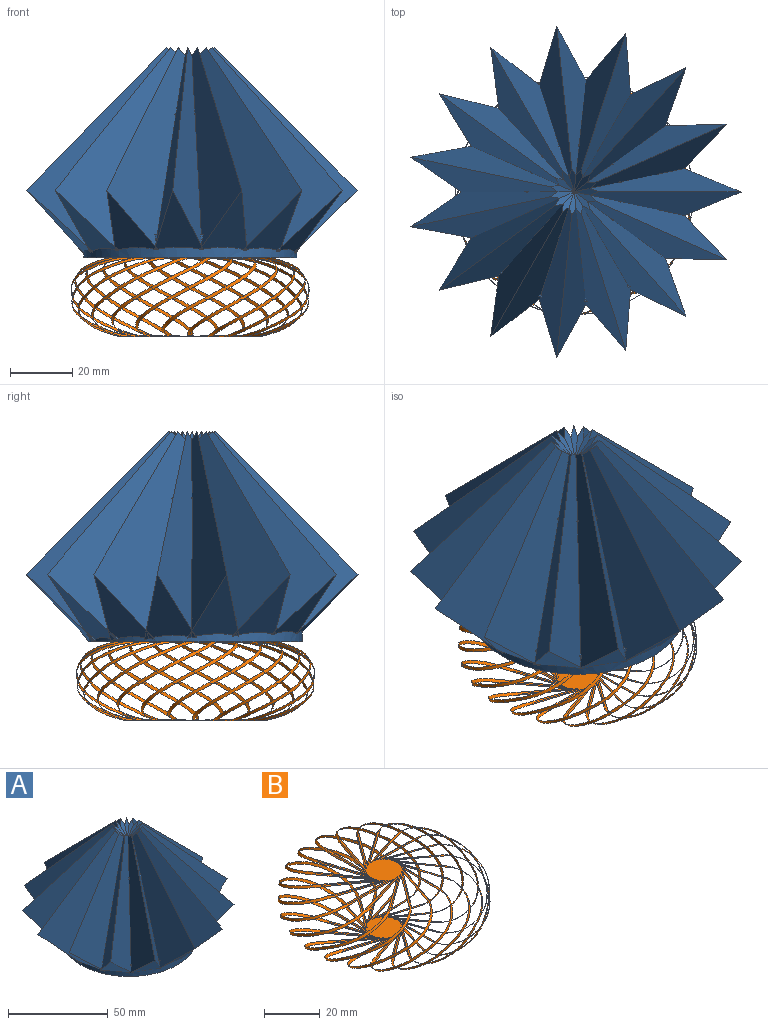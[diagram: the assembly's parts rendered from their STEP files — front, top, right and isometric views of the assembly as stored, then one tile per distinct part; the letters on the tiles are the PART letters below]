
ASSEMBLY  parts=2 mates=1
PART A: 221 faces, bbox 105.8x106.4x67.4 mm
  f0: plane 0.49x0.29mm, normal (-0.47,0.53,-0.71), area 0.1mm2, adj f11,f160,f202
  f1: plane 0.49x0.29mm, normal (-0.47,-0.53,-0.71), area 0.1mm2, adj f12,f46,f200
  f2: plane 0.47x0.29mm, normal (0.57,0.42,-0.71), area 0.1mm2, adj f3,f27,f198
  f3: plane 0.99x0.77mm, normal (0.57,0.42,0.71), area 0.1mm2, adj f2,f26,f198
  f4: plane 0.99x0.77mm, normal (0.57,-0.42,0.71), area 0.1mm2, adj f5,f157,f197
  f5: plane 0.47x0.29mm, normal (0.57,-0.42,-0.71), area 0.1mm2, adj f4,f161,f197
  f6: plane 0.26x0.22mm, normal (0,0,1), area 0mm2, adj f15,f16,f197
  f7: plane 7.69x7.02mm, normal (-0.65,-0.29,0.71), area 11.7mm2, adj f13,f20,f28,f195
  f8: plane 7.69x7.02mm, normal (-0.65,0.29,0.71), area 11.7mm2, adj f15,f91,f117,f195
  f9: plane 63.99x38.53mm, normal (-0.72,0.66,0.2), area 991.9mm2, adj f46,f60,f96,f97,f105,f127,f199,f200
  f10: plane 63.99x38.53mm, normal (-0.72,-0.66,0.2), area 992.1mm2, adj f88,f92,f93,f160,f201,f202
  f11: plane 0.98x0.77mm, normal (-0.47,0.53,0.71), area 0.1mm2, adj f0,f160,f201
  f12: plane 0.98x0.77mm, normal (-0.47,-0.53,0.71), area 0.1mm2, adj f1,f46,f199
  f13: plane 63.99x43.79mm, normal (0.57,-0.8,0.2), area 992.1mm2, adj f7,f14,f20,f26,f27,f198
  f14: plane 20.83x20.43mm, normal (0.65,0.29,-0.71), area 226.8mm2, adj f13,f17,f20,f36,f194
  f15: plane 63.99x43.79mm, normal (0.57,0.8,0.2), area 992mm2, adj f6,f8,f16,f18,f91,f157,f161,f197
  f16: cylinder r=34.13mm len=0.5mm, axis (0,0,-1), area 0.1mm2, adj f6,f15,f197
  f17: cylinder r=34.13mm len=68.25mm, axis (0,0,-1), area 418mm2, adj f14,f18,f19,f21,f29,f35,f36,f38
  f18: plane 20.26x19.65mm, normal (0.65,-0.29,-0.71), area 211.4mm2, adj f15,f17,f91,f152,f192
  f19: plane 2.46x1.93mm, normal (0.57,-0.8,0.2), area 0.7mm2, adj f17,f21,f196
  f20: plane 63.99x44.67mm, normal (-0.21,0.96,0.2), area 992.1mm2, adj f7,f13,f14,f24,f25,f34
  f21: plane 2.48x2.18mm, normal (0.65,0.29,-0.71), area 2.3mm2, adj f17,f19,f193
  f22: plane 0.42x0.29mm, normal (-0.65,0.29,-0.71), area 0.1mm2, adj f31,f111,f188
  f23: plane 0.47x0.29mm, normal (-0.22,-0.67,-0.71), area 0.1mm2, adj f33,f60,f186
  f24: plane 0.49x0.29mm, normal (0.35,0.61,-0.71), area 0.1mm2, adj f20,f25,f43
  f25: plane 0.92x0.77mm, normal (0.35,0.61,0.71), area 0.1mm2, adj f20,f24,f42
  f26: plane 0.89x0.77mm, normal (0.69,-0.15,0.71), area 0.1mm2, adj f3,f13,f27
  f27: plane 0.36x0.33mm, normal (0.69,-0.15,-0.71), area 0.1mm2, adj f2,f13,f26
  f28: plane 7.69x5.71mm, normal (-0.47,-0.53,0.71), area 11.7mm2, adj f7,f34,f37,f44
  f29: plane 2.02x1.58mm, normal (0.57,0.8,0.2), area 0.5mm2, adj f17,f153,f196
  f30: plane 63.99x42.47mm, normal (-0.93,0.31,0.2), area 991.3mm2, adj f60,f74,f98,f99,f100,f132,f185,f186
  f31: plane 0.96x0.77mm, normal (-0.65,0.29,0.71), area 0.1mm2, adj f22,f111,f187
  f32: plane 63.99x47.13mm, normal (-0.39,-0.9,0.2), area 992.1mm2, adj f103,f104,f111,f158,f159,f160,f187,f188
  f33: plane 0.83x0.77mm, normal (-0.22,-0.67,0.71), area 0.1mm2, adj f23,f60,f185
  f34: plane 63.99x36.7mm, normal (0.85,-0.5,0.2), area 992.1mm2, adj f20,f28,f35,f37,f42,f43
  f35: plane 20.71x18.76mm, normal (0.47,0.53,-0.71), area 232.5mm2, adj f17,f34,f37,f50,f190
  f36: plane 3.02x2.96mm, normal (0.85,-0.5,0.2), area 1.1mm2, adj f14,f17,f38
  f37: plane 63.99x35.26mm, normal (-0.58,0.79,0.2), area 992.1mm2, adj f28,f34,f35,f40,f41,f48
  f38: plane 3.02x2.96mm, normal (0.47,0.53,-0.71), area 3.4mm2, adj f17,f36,f189
  f39: plane 0.37x0.33mm, normal (0.07,-0.7,-0.71), area 0.1mm2, adj f47,f74,f181
  f40: plane 0.43x0.29mm, normal (0.07,0.7,-0.71), area 0.1mm2, adj f37,f41,f57
  f41: plane 0.77x0.73mm, normal (0.07,0.7,0.71), area 0.1mm2, adj f37,f40,f56
  f42: plane 0.77x0.77mm, normal (0.69,0.15,0.71), area 0.1mm2, adj f25,f34,f43
  f43: plane 0.45x0.29mm, normal (0.69,0.15,-0.71), area 0.1mm2, adj f24,f34,f42
  f44: plane 7.69x7.31mm, normal (-0.22,-0.67,0.71), area 11.7mm2, adj f28,f48,f51,f58
  f45: plane 63.99x48.26mm, normal (-0.98,-0.1,0.2), area 990.7mm2, adj f74,f90,f101,f102,f108,f137,f180,f181
  f46: plane 63.99x47.58mm, normal (0.01,-0.98,0.2), area 991.9mm2, adj f1,f9,f12,f96,f97,f111,f112,f122
  f47: plane 0.83x0.77mm, normal (0.07,-0.7,0.71), area 0.1mm2, adj f39,f74,f180
  f48: plane 63.99x46.38mm, normal (0.97,-0.11,0.2), area 992.1mm2, adj f37,f44,f49,f51,f56,f57
  f49: plane 21.3x20.86mm, normal (0.22,0.67,-0.71), area 235.8mm2, adj f17,f48,f51,f64,f184
  f50: plane 3.6x3.34mm, normal (0.97,-0.11,0.2), area 1.3mm2, adj f17,f35,f52
  f51: plane 63.99x45.71mm, normal (-0.85,0.48,0.2), area 992.1mm2, adj f44,f48,f49,f54,f55,f62
  f52: plane 3.6x3.34mm, normal (0.22,0.67,-0.71), area 4.2mm2, adj f17,f50,f182
  f53: plane 0.45x0.29mm, normal (0.35,-0.61,-0.71), area 0.1mm2, adj f61,f90,f176
  f54: plane 0.4x0.29mm, normal (-0.22,0.67,-0.71), area 0.1mm2, adj f51,f55,f72
  f55: plane 0.93x0.77mm, normal (-0.22,0.67,0.71), area 0.1mm2, adj f51,f54,f71
  f56: plane 0.95x0.77mm, normal (0.57,0.42,0.71), area 0.1mm2, adj f41,f48,f57
  f57: plane 0.49x0.29mm, normal (0.57,0.42,-0.71), area 0.1mm2, adj f40,f48,f56
  f58: plane 7.69x7.64mm, normal (0.07,-0.7,0.71), area 11.7mm2, adj f44,f62,f66,f73
  f59: plane 63.99x45.71mm, normal (-0.85,-0.48,0.2), area 990.6mm2, adj f90,f106,f107,f113,f142,f147,f175,f176
  f60: plane 63.99x39.8mm, normal (0.4,-0.89,0.2), area 991.3mm2, adj f9,f23,f30,f33,f98,f99,f105,f127
  f61: plane 0.98x0.77mm, normal (0.35,-0.61,0.71), area 0.1mm2, adj f53,f90,f175
  f62: plane 63.99x48.04mm, normal (0.93,0.3,0.2), area 992.1mm2, adj f51,f58,f63,f66,f71,f72
  f63: plane 21.24x20.87mm, normal (-0.07,0.7,-0.71), area 236.5mm2, adj f17,f62,f66,f80,f179
  f64: plane 3.36x3.35mm, normal (0.93,0.3,0.2), area 1.5mm2, adj f17,f49,f65,f67
  f65: plane 0.6x0.16mm, normal (0.07,-0.7,-0.71), area 0.1mm2, adj f17,f64,f67
  f66: plane 63.99x48.26mm, normal (-0.98,0.1,0.2), area 992.1mm2, adj f58,f62,f63,f69,f70,f77
  f67: plane 3.38x3.28mm, normal (-0.07,0.7,-0.71), area 4.6mm2, adj f17,f64,f65,f177
  f68: plane 0.49x0.29mm, normal (0.57,-0.42,-0.71), area 0.1mm2, adj f76,f147,f171
  f69: plane 0.48x0.29mm, normal (-0.47,0.53,-0.71), area 0.1mm2, adj f66,f70,f87
  f70: plane 0.99x0.77mm, normal (-0.47,0.53,0.71), area 0.1mm2, adj f66,f69,f86
  f71: plane 0.98x0.77mm, normal (0.35,0.61,0.71), area 0.1mm2, adj f55,f62,f72
  f72: plane 0.45x0.29mm, normal (0.35,0.61,-0.71), area 0.1mm2, adj f54,f62,f71
  f73: plane 7.69x6.66mm, normal (0.35,-0.61,0.71), area 11.7mm2, adj f58,f77,f79,f88
  f74: plane 63.99x41.39mm, normal (0.73,-0.65,0.2), area 990.7mm2, adj f30,f39,f45,f47,f100,f101,f102,f132
  f75: plane 63.99x35.26mm, normal (-0.58,-0.79,0.2), area 991mm2, adj f114,f115,f116,f117,f147,f148,f170,f171
  f76: plane 0.95x0.77mm, normal (0.57,-0.42,0.71), area 0.1mm2, adj f68,f147,f170
  f77: plane 63.99x41.39mm, normal (0.73,0.65,0.2), area 992.1mm2, adj f66,f73,f78,f79,f86,f87
  f78: plane 20.8x20.45mm, normal (-0.35,0.61,-0.71), area 234.5mm2, adj f17,f77,f79,f94,f174
  f79: plane 63.99x42.47mm, normal (-0.93,-0.31,0.2), area 992.1mm2, adj f73,f77,f78,f84,f85,f92
  f80: plane 3.36x2.95mm, normal (0.73,0.65,0.2), area 1.5mm2, adj f17,f63,f81,f82
  f81: plane 0.48x0.24mm, normal (0.35,-0.61,-0.71), area 0mm2, adj f17,f80,f82
  f82: plane 3.38x2.92mm, normal (-0.35,0.61,-0.71), area 4.5mm2, adj f17,f80,f81,f172
  f83: plane 0.45x0.29mm, normal (0.69,-0.15,-0.71), area 0.1mm2, adj f89,f114,f167
  f84: plane 0.48x0.29mm, normal (-0.65,0.29,-0.71), area 0.1mm2, adj f79,f85,f162
  f85: plane 0.88x0.77mm, normal (-0.65,0.29,0.71), area 0.1mm2, adj f79,f84,f163
  f86: plane 0.83x0.77mm, normal (0.07,0.7,0.71), area 0.1mm2, adj f70,f77,f87
  f87: plane 0.37x0.33mm, normal (0.07,0.7,-0.71), area 0.1mm2, adj f69,f77,f86
  f88: plane 7.69x6.22mm, normal (0.57,-0.42,0.71), area 11.7mm2, adj f10,f73,f92,f159
  f89: plane 0.77x0.77mm, normal (0.69,-0.15,0.71), area 0.1mm2, adj f83,f114,f166
  f90: plane 63.99x48.04mm, normal (0.93,-0.3,0.2), area 990.6mm2, adj f45,f53,f59,f61,f106,f107,f108,f137
  f91: plane 63.99x44.67mm, normal (-0.21,-0.96,0.2), area 991.6mm2, adj f8,f15,f18,f109,f110,f114,f166,f167
  f92: plane 63.99x39.8mm, normal (0.4,0.89,0.2), area 992.1mm2, adj f10,f79,f88,f93,f162,f163
  f93: plane 20.58x19.7mm, normal (-0.57,0.42,-0.71), area 229.9mm2, adj f10,f17,f92,f156,f169
  f94: plane 3.44x3.27mm, normal (0.4,0.89,0.2), area 1.3mm2, adj f17,f78,f95
  f95: plane 3.44x3.27mm, normal (-0.57,0.42,-0.71), area 4mm2, adj f17,f94,f168
  f96: cylinder r=34.13mm len=0.95mm, axis (0,0,-1), area 0.2mm2, adj f9,f46,f97
  f97: plane 0.52x0.39mm, normal (0,0,1), area 0.1mm2, adj f9,f46,f96
  f98: cylinder r=34.13mm len=1.73mm, axis (0,0,-1), area 0.7mm2, adj f30,f60,f99
  f99: plane 0.91x0.86mm, normal (0,0,1), area 0.3mm2, adj f30,f60,f98
  f100: plane 7.69x6.66mm, normal (0.35,0.61,0.71), area 11.7mm2, adj f30,f74,f105,f108
  f101: cylinder r=34.13mm len=2.22mm, axis (0,0,-1), area 1.1mm2, adj f45,f74,f102
  f102: plane 1.22x0.93mm, normal (0,0,1), area 0.5mm2, adj f45,f74,f101
  f103: plane 0.01x0.01mm, normal (0,0,1), area 0mm2, adj f32,f104,f111
  f104: cylinder r=34.13mm len=0.02mm, axis (0,0,-1), area 0mm2, adj f32,f103,f111
  f105: plane 7.69x6.22mm, normal (0.57,0.42,0.71), area 11.7mm2, adj f9,f60,f100,f112
  f106: cylinder r=34.13mm len=2.32mm, axis (0,0,-1), area 1.2mm2, adj f59,f90,f107
  f107: plane 1.21x1.01mm, normal (0,0,1), area 0.6mm2, adj f59,f90,f106
  f108: plane 7.69x7.64mm, normal (0.07,0.7,0.71), area 11.7mm2, adj f45,f90,f100,f113
  f109: cylinder r=34.13mm len=1.37mm, axis (0,0,-1), area 0.4mm2, adj f91,f110,f114
  f110: plane 0.73x0.66mm, normal (0,0,1), area 0.2mm2, adj f91,f109,f114
  f111: plane 63.99x47.13mm, normal (-0.39,0.9,0.2), area 992.1mm2, adj f22,f31,f32,f46,f103,f104,f112,f122
  f112: plane 7.69x7.52mm, normal (0.69,0.15,0.71), area 11.7mm2, adj f46,f105,f111,f159
  f113: plane 7.69x7.31mm, normal (-0.22,0.67,0.71), area 11.7mm2, adj f59,f108,f117,f147
  f114: plane 63.99x36.7mm, normal (0.85,0.5,0.2), area 991.6mm2, adj f75,f83,f89,f91,f109,f110,f117,f148
  f115: cylinder r=34.13mm len=2.02mm, axis (0,0,-1), area 0.9mm2, adj f75,f116,f147
  f116: plane 1.11x0.89mm, normal (0,0,1), area 0.5mm2, adj f75,f115,f147
  f117: plane 7.69x5.71mm, normal (-0.47,0.53,0.71), area 11.7mm2, adj f8,f75,f113,f114
  f118: plane 2.3x2.05mm, normal (-0.39,0.9,0.2), area 0.6mm2, adj f17,f119,f158
  f119: plane 2.32x2.07mm, normal (-0.69,-0.15,-0.71), area 2mm2, adj f17,f118,f120
  f120: plane 2.21x1.99mm, normal (-0.69,0.15,-0.71), area 1.9mm2, adj f17,f119,f121
  f121: plane 2.19x1.96mm, normal (-0.39,-0.9,0.2), area 0.6mm2, adj f17,f120,f122
  f122: plane 20.37x19.85mm, normal (-0.69,-0.15,-0.71), area 215.4mm2, adj f17,f46,f111,f121,f123
  f123: plane 1.75x1.61mm, normal (-0.72,0.66,0.2), area 0.4mm2, adj f17,f122,f124
  f124: plane 1.75x1.62mm, normal (-0.57,-0.42,-0.71), area 1.1mm2, adj f17,f123,f125
  f125: plane 1.79x1.68mm, normal (-0.69,-0.15,-0.71), area 1.1mm2, adj f17,f124,f126
  f126: plane 1.78x1.67mm, normal (0.01,-0.98,0.2), area 0.3mm2, adj f17,f125,f127
  f127: plane 19.46x19.36mm, normal (-0.57,-0.42,-0.71), area 207.6mm2, adj f9,f17,f60,f126,f128
  f128: plane 1.37x1.28mm, normal (-0.93,0.31,0.2), area 0.2mm2, adj f17,f127,f129
  f129: plane 1.38x1.28mm, normal (-0.35,-0.61,-0.71), area 0.6mm2, adj f17,f128,f130
  f130: plane 1.31x1.25mm, normal (-0.57,-0.42,-0.71), area 0.6mm2, adj f17,f129,f131
  f131: plane 1.31x1.24mm, normal (0.4,-0.89,0.2), area 0.2mm2, adj f17,f130,f132
  f132: plane 19.86x19.13mm, normal (-0.35,-0.61,-0.71), area 201.6mm2, adj f17,f30,f74,f131,f133
  f133: plane 1.03x0.99mm, normal (-0.98,-0.1,0.2), area 0.1mm2, adj f17,f132,f134
  f134: plane 1.03x0.99mm, normal (-0.07,-0.7,-0.71), area 0.4mm2, adj f17,f133,f135
  f135: plane 0.98x0.84mm, normal (-0.35,-0.61,-0.71), area 0.4mm2, adj f17,f134,f136
  f136: plane 0.98x0.84mm, normal (0.73,-0.65,0.2), area 0.1mm2, adj f17,f135,f137
  f137: plane 19.53x18.93mm, normal (-0.07,-0.7,-0.71), area 198.7mm2, adj f17,f45,f90,f136,f138
  f138: plane 0.92x0.76mm, normal (-0.85,-0.48,0.2), area 0.1mm2, adj f17,f137,f139
  f139: plane 0.92x0.82mm, normal (0.22,-0.67,-0.71), area 0.3mm2, adj f17,f138,f140
  f140: plane 0.93x0.88mm, normal (-0.07,-0.7,-0.71), area 0.3mm2, adj f17,f139,f141
  f141: plane 0.93x0.88mm, normal (0.93,-0.3,0.2), area 0.1mm2, adj f17,f140,f142
  f142: plane 20.15x19.01mm, normal (0.22,-0.67,-0.71), area 199.7mm2, adj f17,f59,f141,f143,f147
  f143: plane 1.08x1.06mm, normal (-0.58,-0.79,0.2), area 0.1mm2, adj f17,f142,f144
  f144: plane 1.09x1.06mm, normal (0.47,-0.53,-0.71), area 0.5mm2, adj f17,f143,f145
  f145: plane 1.2x1.11mm, normal (0.22,-0.67,-0.71), area 0.5mm2, adj f17,f144,f146
  f146: plane 1.2x1.11mm, normal (0.97,0.11,0.2), area 0.1mm2, adj f17,f145,f148
  f147: plane 63.99x46.38mm, normal (0.97,0.11,0.2), area 991mm2, adj f59,f68,f75,f76,f113,f115,f116,f142
  f148: plane 19.28x18.64mm, normal (0.47,-0.53,-0.71), area 204.3mm2, adj f17,f75,f114,f146,f149
  f149: plane 1.56x1.44mm, normal (-0.21,-0.96,0.2), area 0.3mm2, adj f17,f148,f150
  f150: plane 1.56x1.45mm, normal (0.65,-0.29,-0.71), area 0.8mm2, adj f17,f149,f151
  f151: plane 1.53x1.5mm, normal (0.47,-0.53,-0.71), area 0.8mm2, adj f17,f150,f152
  f152: plane 1.52x1.5mm, normal (0.85,0.5,0.2), area 0.3mm2, adj f17,f18,f151
  f153: plane 2.03x1.71mm, normal (0.65,-0.29,-0.71), area 1.5mm2, adj f17,f29,f191
  f154: plane 68.25x68.25mm, normal (0,0,-1), area 3658.9mm2, adj f17
  f155: plane 3.02x2.84mm, normal (-0.69,0.15,-0.71), area 3mm2, adj f17,f156,f164
  f156: plane 3.03x2.84mm, normal (0.01,0.98,0.2), area 1mm2, adj f17,f93,f155
  f157: plane 0.89x0.77mm, normal (0.69,0.15,0.71), area 0.1mm2, adj f4,f15,f161
  f158: plane 20.95x20.25mm, normal (-0.69,0.15,-0.71), area 223.3mm2, adj f17,f32,f118,f160,f165
  f159: plane 7.69x7.52mm, normal (0.69,-0.15,0.71), area 11.7mm2, adj f32,f88,f112,f160
  f160: plane 63.99x47.58mm, normal (0.01,0.98,0.2), area 992.1mm2, adj f0,f10,f11,f32,f158,f159
  f161: plane 0.36x0.33mm, normal (0.69,0.15,-0.71), area 0.1mm2, adj f5,f15,f157
  f162: plane 0.47x0.29mm, normal (-0.22,0.67,-0.71), area 0.1mm2, adj f84,f92,f163
  f163: plane 0.83x0.77mm, normal (-0.22,0.67,0.71), area 0.1mm2, adj f85,f92,f162
  f164: plane 2.74x2.53mm, normal (-0.57,0.42,-0.71), area 2.9mm2, adj f17,f155,f165
  f165: plane 2.72x2.51mm, normal (-0.72,-0.66,0.2), area 0.9mm2, adj f17,f158,f164
  f166: plane 0.92x0.77mm, normal (0.35,-0.61,0.71), area 0.1mm2, adj f89,f91,f167
  f167: plane 0.49x0.29mm, normal (0.35,-0.61,-0.71), area 0.1mm2, adj f83,f91,f166
  f168: plane 3.4x3.17mm, normal (-0.35,0.61,-0.71), area 3.8mm2, adj f17,f95,f169
  f169: plane 3.4x3.17mm, normal (-0.93,-0.31,0.2), area 1.2mm2, adj f17,f93,f168
  f170: plane 0.77x0.73mm, normal (0.07,-0.7,0.71), area 0.1mm2, adj f75,f76,f171
  f171: plane 0.43x0.29mm, normal (0.07,-0.7,-0.71), area 0.1mm2, adj f68,f75,f170
  f172: plane 3.49x3.36mm, normal (-0.07,0.7,-0.71), area 4.5mm2, adj f17,f82,f173,f174
  f173: plane 0.34x0.13mm, normal (0.07,-0.7,-0.71), area 0mm2, adj f17,f172,f174
  f174: plane 3.58x3.36mm, normal (-0.98,0.1,0.2), area 1.4mm2, adj f17,f78,f172,f173
  f175: plane 0.93x0.77mm, normal (-0.22,-0.67,0.71), area 0.1mm2, adj f59,f61,f176
  f176: plane 0.4x0.29mm, normal (-0.22,-0.67,-0.71), area 0.1mm2, adj f53,f59,f175
  f177: plane 3.38x3.09mm, normal (0.22,0.67,-0.71), area 4.6mm2, adj f17,f67,f178,f179
  f178: plane 0.65x0.2mm, normal (-0.22,-0.67,-0.71), area 0.1mm2, adj f17,f177,f179
  f179: plane 3.36x2.94mm, normal (-0.85,0.48,0.2), area 1.5mm2, adj f17,f63,f177,f178
  f180: plane 0.99x0.77mm, normal (-0.47,-0.53,0.71), area 0.1mm2, adj f45,f47,f181
  f181: plane 0.48x0.29mm, normal (-0.47,-0.53,-0.71), area 0.1mm2, adj f39,f45,f180
  f182: plane 3.36x3.28mm, normal (0.47,0.53,-0.71), area 4.3mm2, adj f17,f52,f183,f184
  f183: plane 0.16x0.12mm, normal (-0.47,-0.53,-0.71), area 0mm2, adj f17,f182,f184
  f184: plane 3.36x3.32mm, normal (-0.58,0.79,0.2), area 1.4mm2, adj f17,f49,f182,f183
  f185: plane 0.88x0.77mm, normal (-0.65,-0.29,0.71), area 0.1mm2, adj f30,f33,f186
  f186: plane 0.48x0.29mm, normal (-0.65,-0.29,-0.71), area 0.1mm2, adj f23,f30,f185
  f187: plane 0.96x0.77mm, normal (-0.65,-0.29,0.71), area 0.1mm2, adj f31,f32,f188
  f188: plane 0.42x0.29mm, normal (-0.65,-0.29,-0.71), area 0.1mm2, adj f22,f32,f187
  f189: plane 3.33x3.08mm, normal (0.65,0.29,-0.71), area 3.5mm2, adj f17,f38,f190
  f190: plane 3.33x3.08mm, normal (-0.21,0.96,0.2), area 1.1mm2, adj f17,f35,f189
  f191: plane 1.94x1.94mm, normal (0.71,0,-0.71), area 1.4mm2, adj f17,f153,f192
  f192: plane 1.93x1.93mm, normal (0.2,-0.96,0.2), area 0.4mm2, adj f17,f18,f191
  f193: plane 2.6x2.6mm, normal (0.71,0,-0.71), area 2.5mm2, adj f17,f21,f194
  f194: plane 2.58x2.58mm, normal (0.2,0.96,0.2), area 0.8mm2, adj f14,f17,f193
  f195: plane 7.69x7.69mm, normal (-0.71,0,0.71), area 11.7mm2, adj f7,f8,f197,f198
  f196: plane 20.05x20.05mm, normal (0.71,0,-0.71), area 219.4mm2, adj f17,f19,f29,f197,f198
  f197: plane 63.99x48.41mm, normal (0.2,-0.96,0.2), area 992.1mm2, adj f4,f5,f6,f15,f16,f195,f196,f198
  f198: plane 63.99x48.41mm, normal (0.2,0.96,0.2), area 992.1mm2, adj f2,f3,f13,f195,f196,f197
  f199: plane 0.77x0.77mm, normal (-0.71,0,0.71), area 0.1mm2, adj f9,f12,f200
  f200: plane 0.4x0.29mm, normal (-0.71,0,-0.71), area 0.1mm2, adj f1,f9,f199
  f201: plane 0.77x0.77mm, normal (-0.71,0,0.71), area 0.1mm2, adj f10,f11,f202
  f202: plane 0.4x0.29mm, normal (-0.71,0,-0.71), area 0.1mm2, adj f0,f10,f201
  f203: cylinder r=19.05mm len=38.1mm, axis (0,0,-1), area 531.2mm2, adj f204,f205,f206,f208,f209,f210,f211,f212
  f204: plane 10.47x5.99mm, normal (-0.71,0,-0.71), area 74.7mm2, adj f203,f206,f207,f208
  f205: plane 38.1x38.1mm, normal (0,0,-1), area 1140.1mm2, adj f203
  f206: plane 10.83x9.21mm, normal (-0.65,0.29,-0.71), area 74.7mm2, adj f203,f204,f207,f212
  f207: plane 50.06x49.79mm, normal (0,0,1), area 1932.4mm2, adj f204,f206,f208,f209,f210,f211,f212,f213
  f208: plane 10.83x9.21mm, normal (-0.65,-0.29,-0.71), area 74.7mm2, adj f203,f204,f207,f220
  f209: plane 10.24x7.77mm, normal (0.69,0.15,-0.71), area 74.7mm2, adj f203,f207,f214,f215
  f210: plane 10.95x9.78mm, normal (0.35,0.61,-0.71), area 74.7mm2, adj f203,f207,f211,f214
  f211: plane 10.41x6.91mm, normal (0.07,0.7,-0.71), area 74.7mm2, adj f203,f207,f210,f213
  f212: plane 10.84x10.6mm, normal (-0.47,0.53,-0.71), area 74.7mm2, adj f203,f206,f207,f213
  f213: plane 10.59x8.53mm, normal (-0.22,0.67,-0.71), area 74.7mm2, adj f203,f207,f211,f212
  f214: plane 10.96x10.25mm, normal (0.57,0.42,-0.71), area 74.7mm2, adj f203,f207,f209,f210
  f215: plane 10.24x7.77mm, normal (0.69,-0.15,-0.71), area 74.7mm2, adj f203,f207,f209,f216
  f216: plane 10.96x10.25mm, normal (0.57,-0.42,-0.71), area 74.7mm2, adj f203,f207,f215,f217
  f217: plane 10.95x9.78mm, normal (0.35,-0.61,-0.71), area 74.7mm2, adj f203,f207,f216,f218
  f218: plane 10.41x6.91mm, normal (0.07,-0.7,-0.71), area 74.7mm2, adj f203,f207,f217,f219
  f219: plane 10.59x8.53mm, normal (-0.22,-0.67,-0.71), area 74.7mm2, adj f203,f207,f218,f220
  f220: plane 10.84x10.6mm, normal (-0.47,-0.53,-0.71), area 74.7mm2, adj f203,f207,f208,f219
PART B: 126 faces, bbox 82.8x82.8x43.6 mm
  f0: bspline ~23.09x1.02mm, area 7mm2, adj f39,f121
  f1: bspline ~22.22x7.95mm, area 7mm2, adj f38,f121
  f2: bspline ~22.22x7.95mm, area 7mm2, adj f20,f121
  f3: bspline ~19.18x14.26mm, area 7mm2, adj f21,f121
  f4: bspline ~19.18x14.26mm, area 7mm2, adj f22,f121
  f5: bspline ~22.22x7.95mm, area 7mm2, adj f23,f121
  f6: bspline ~23.09x1.02mm, area 7mm2, adj f24,f121
  f7: bspline ~22.22x7.95mm, area 7mm2, adj f25,f121
  f8: bspline ~19.18x14.26mm, area 7mm2, adj f26,f121
  f9: bspline ~19.18x14.26mm, area 7mm2, adj f27,f121
  f10: bspline ~22.22x7.95mm, area 7mm2, adj f28,f121
  f11: bspline ~23.09x1.02mm, area 7mm2, adj f29,f121
  f12: bspline ~22.22x7.95mm, area 7mm2, adj f30,f121
  f13: bspline ~19.18x14.26mm, area 7mm2, adj f31,f121
  f14: bspline ~19.18x14.26mm, area 7mm2, adj f32,f121
  f15: bspline ~22.22x7.95mm, area 7mm2, adj f33,f121
  f16: bspline ~23.09x1.02mm, area 7mm2, adj f34,f121
  f17: bspline ~22.22x7.95mm, area 7mm2, adj f35,f121
  f18: bspline ~19.18x14.26mm, area 7mm2, adj f36,f121
  f19: bspline ~19.18x14.26mm, area 7mm2, adj f37,f121
  f20: bspline ~25.52x24.34mm, area 33.5mm2, adj f2,f102,f121
  f21: bspline ~25.52x23.85mm, area 33.5mm2, adj f3,f103,f121
  f22: bspline ~25.52x23.45mm, area 33.5mm2, adj f4,f104,f121
  f23: bspline ~25.52x24.85mm, area 33.5mm2, adj f5,f105,f121
  f24: bspline ~25.52x24.23mm, area 33.5mm2, adj f6,f106,f121
  f25: bspline ~25.52x24.34mm, area 33.5mm2, adj f7,f107,f121
  f26: bspline ~25.52x23.85mm, area 33.5mm2, adj f8,f108,f121
  f27: bspline ~25.52x23.45mm, area 33.5mm2, adj f9,f109,f121
  f28: bspline ~25.52x24.85mm, area 33.5mm2, adj f10,f110,f121
  f29: bspline ~25.52x24.23mm, area 33.5mm2, adj f11,f111,f121
  f30: bspline ~25.52x24.34mm, area 33.5mm2, adj f12,f112,f121
  f31: bspline ~25.52x23.85mm, area 33.5mm2, adj f13,f113,f121
  f32: bspline ~25.52x23.45mm, area 33.5mm2, adj f14,f114,f121
  f33: bspline ~25.52x24.85mm, area 33.5mm2, adj f15,f115,f121
  f34: bspline ~25.52x24.23mm, area 33.5mm2, adj f16,f116,f121
  f35: bspline ~25.52x24.34mm, area 33.5mm2, adj f17,f117,f121
  f36: bspline ~25.52x23.85mm, area 33.5mm2, adj f18,f118,f121
  f37: bspline ~25.52x23.45mm, area 33.5mm2, adj f19,f119,f121
  f38: bspline ~25.52x24.85mm, area 33.5mm2, adj f1,f101,f121
  f39: bspline ~25.52x24.23mm, area 33.5mm2, adj f0,f100,f121
  f40: bspline ~31.61x10.94mm, area 9.3mm2, adj f58,f99,f120
  f41: bspline ~32.98x1.02mm, area 9.3mm2, adj f78,f98,f120
  f42: bspline ~0.3x0.11mm, area 0mm2, adj f74,f120
  f43: bspline ~3.55x1.68mm, area 0mm2, adj f73,f120
  f44: bspline ~3.55x1.66mm, area 0mm2, adj f72,f120
  f45: bspline ~0.28x0.12mm, area 0mm2, adj f71,f120
  f46: bspline ~3.55x1.25mm, area 0mm2, adj f70,f120
  f47: bspline ~0.3x0.11mm, area 0mm2, adj f69,f120
  f48: bspline ~3.55x1.68mm, area 0mm2, adj f68,f120
  f49: bspline ~3.55x1.66mm, area 0mm2, adj f67,f120
  f50: bspline ~0.28x0.12mm, area 0mm2, adj f66,f120
  f51: bspline ~3.55x1.25mm, area 0mm2, adj f65,f120
  f52: bspline ~0.3x0.11mm, area 0mm2, adj f64,f120
  f53: bspline ~3.55x1.68mm, area 0mm2, adj f63,f120
  f54: bspline ~3.55x1.66mm, area 0mm2, adj f62,f120
  f55: bspline ~0.28x0.12mm, area 0mm2, adj f61,f120
  f56: bspline ~3.55x1.25mm, area 0mm2, adj f60,f120
  f57: bspline ~0.3x0.11mm, area 0mm2, adj f59,f120
  f58: bspline ~3.55x1.68mm, area 0mm2, adj f40,f120
  f59: bspline ~27.14x20.02mm, area 9.3mm2, adj f57,f80,f120
  f60: bspline ~27.15x20.02mm, area 9.3mm2, adj f56,f81,f120
  f61: bspline ~31.61x10.94mm, area 9.3mm2, adj f55,f82,f120
  f62: bspline ~32.98x1.02mm, area 9.3mm2, adj f54,f83,f120
  f63: bspline ~31.61x10.94mm, area 9.3mm2, adj f53,f84,f120
  f64: bspline ~27.14x20.02mm, area 9.3mm2, adj f52,f85,f120
  f65: bspline ~27.15x20.02mm, area 9.3mm2, adj f51,f86,f120
  f66: bspline ~31.61x10.94mm, area 9.3mm2, adj f50,f87,f120
  f67: bspline ~32.98x1.02mm, area 9.3mm2, adj f49,f88,f120
  f68: bspline ~31.61x10.94mm, area 9.3mm2, adj f48,f89,f120
  f69: bspline ~27.14x20.02mm, area 9.3mm2, adj f47,f90,f120
  f70: bspline ~27.15x20.02mm, area 9.3mm2, adj f46,f91,f120
  f71: bspline ~31.61x10.94mm, area 9.3mm2, adj f45,f92,f120
  f72: bspline ~32.98x1.02mm, area 9.3mm2, adj f44,f93,f120
  f73: bspline ~31.61x10.94mm, area 9.3mm2, adj f43,f94,f120
  f74: bspline ~27.14x20.02mm, area 9.3mm2, adj f42,f95,f120
  f75: bspline ~27.15x20.02mm, area 9.3mm2, adj f77,f96,f120
  f76: bspline ~31.61x10.94mm, area 9.3mm2, adj f79,f97,f120
  f77: bspline ~3.55x1.25mm, area 0mm2, adj f75,f120
  f78: bspline ~3.55x1.66mm, area 0mm2, adj f41,f120
  f79: bspline ~0.28x0.12mm, area 0mm2, adj f76,f120
  f80: bspline ~24.6x18.42mm, area 29.9mm2, adj f59,f102,f120
  f81: bspline ~23.34x18.42mm, area 29.9mm2, adj f60,f103,f120
  f82: bspline ~20.94x18.42mm, area 29.9mm2, adj f61,f104,f120
  f83: bspline ~20.78x20.34mm, area 29.9mm2, adj f62,f105,f120
  f84: bspline ~23.86x19.11mm, area 29.9mm2, adj f63,f106,f120
  f85: bspline ~24.6x18.42mm, area 29.9mm2, adj f64,f107,f120
  f86: bspline ~23.34x18.42mm, area 29.9mm2, adj f65,f108,f120
  f87: bspline ~20.94x18.42mm, area 29.9mm2, adj f66,f109,f120
  f88: bspline ~20.78x20.34mm, area 29.9mm2, adj f67,f110,f120
  f89: bspline ~23.86x19.11mm, area 29.9mm2, adj f68,f111,f120
  f90: bspline ~24.6x18.42mm, area 29.9mm2, adj f69,f112,f120
  f91: bspline ~23.34x18.42mm, area 29.9mm2, adj f70,f113,f120
  f92: bspline ~20.94x18.42mm, area 29.9mm2, adj f71,f114,f120
  f93: bspline ~20.78x20.34mm, area 29.9mm2, adj f72,f115,f120
  f94: bspline ~23.86x19.11mm, area 29.9mm2, adj f73,f116,f120
  f95: bspline ~24.6x18.42mm, area 29.9mm2, adj f74,f117,f120
  f96: bspline ~23.34x18.42mm, area 29.9mm2, adj f75,f118,f120
  f97: bspline ~20.94x18.42mm, area 29.9mm2, adj f76,f119,f120
  f98: bspline ~20.78x20.34mm, area 29.9mm2, adj f41,f101,f120
  f99: bspline ~23.86x19.11mm, area 29.9mm2, adj f40,f100,f120
  f100: bspline ~5.86x5.35mm, area 7.7mm2, adj f39,f99
  f101: bspline ~7.23x4.85mm, area 7.7mm2, adj f38,f98
  f102: bspline ~13.62x8.83mm, area 7.7mm2, adj f20,f80
  f103: bspline ~7.77x4.85mm, area 7.7mm2, adj f21,f81
  f104: bspline ~7.89x4.85mm, area 7.7mm2, adj f22,f82
  f105: bspline ~7.23x4.85mm, area 7.7mm2, adj f23,f83
  f106: bspline ~5.86x5.35mm, area 7.7mm2, adj f24,f84
  f107: bspline ~13.62x8.83mm, area 7.7mm2, adj f25,f85
  f108: bspline ~7.77x4.85mm, area 7.7mm2, adj f26,f86
  f109: bspline ~7.89x4.85mm, area 7.7mm2, adj f27,f87
  f110: bspline ~7.23x4.85mm, area 7.7mm2, adj f28,f88
  f111: bspline ~5.86x5.35mm, area 7.7mm2, adj f29,f89
  f112: bspline ~13.62x8.83mm, area 7.7mm2, adj f30,f90
  f113: bspline ~7.77x4.85mm, area 7.7mm2, adj f31,f91
  f114: bspline ~7.89x4.85mm, area 7.7mm2, adj f32,f92
  f115: bspline ~7.23x4.85mm, area 7.7mm2, adj f33,f93
  f116: bspline ~5.86x5.35mm, area 7.7mm2, adj f34,f94
  f117: bspline ~13.62x8.83mm, area 7.7mm2, adj f35,f95
  f118: bspline ~7.77x4.85mm, area 7.7mm2, adj f36,f96
  f119: bspline ~7.89x4.85mm, area 7.7mm2, adj f37,f97
  f120: plane 51.66x51.66mm, normal (0,0,1), area 398.9mm2, adj f40,f41,f42,f43,f44,f45,f46,f47
  f121: plane 44.02x44.02mm, normal (0,0,-1), area 343.6mm2, adj f0,f1,f2,f3,f4,f5,f6,f7
  f122: bspline ~5.93x4.69mm, area 0mm2, adj f121
  f123: bspline ~5.93x4.69mm, area 0mm2, adj f121
  f124: bspline ~5.93x4.69mm, area 0mm2, adj f121
  f125: bspline ~5.93x4.69mm, area 0mm2, adj f121
PLACE A t=(12.99,-65.9,39.68)mm
PLACE B t=(12.99,-67.04,5.65)mm
MATE revolute A.f16 <-> B.f120  axis (0,0,-1) through (12.99,-67.04,31.05)mm
